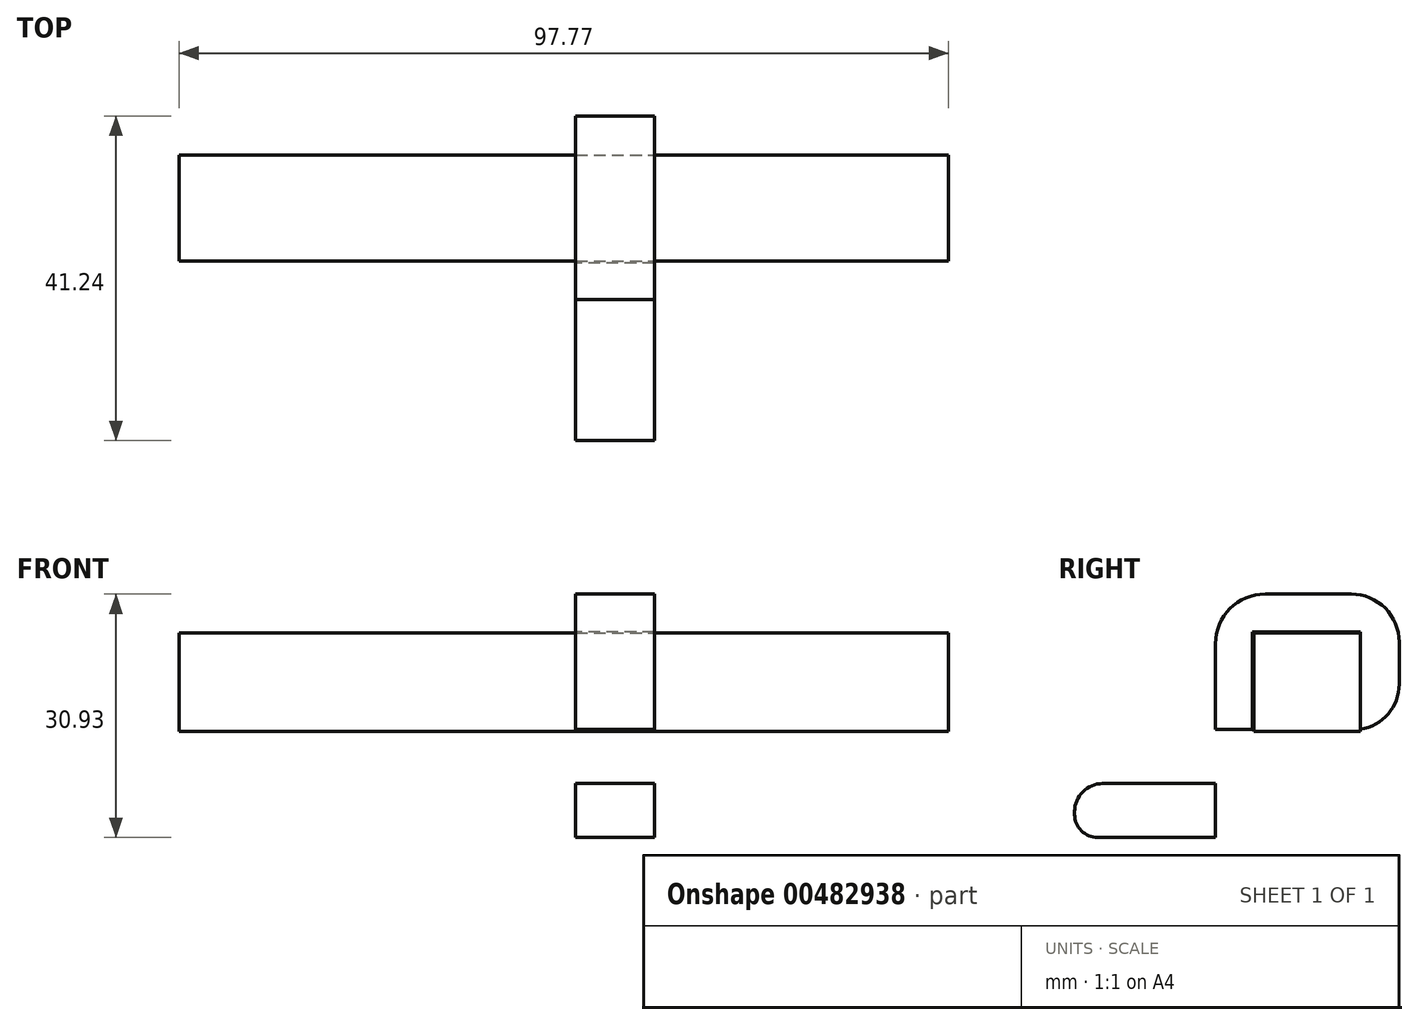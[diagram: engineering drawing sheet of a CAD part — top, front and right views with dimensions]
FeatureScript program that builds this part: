
annotation { "Feature Type Name" : "Feature", "Feature Type Description" : "" }
export const myFeature = defineFeature(function(context is Context, id is Id, definition is map)
    precondition{}
    {
        {
            var Q0;
            Q0=qCreatedBy(makeId("Front.planeOp"),FACE);
            var sketch = newSketch(context, id + "F0", { "sketchPlane" : qUnion([Q0])});
            skLineSegment(sketch, "E0.bottom", {"start": v(-50.4, 26) * mm, "end": v(47.37, 26) * mm});
            skLineSegment(sketch, "E0.top", {"start": v(-50.4, 0) * mm, "end": v(47.37, 0) * mm});
            skLineSegment(sketch, "E0.left", {"start": v(-50.4, 26) * mm, "end": v(-50.4, 0) * mm});
            skLineSegment(sketch, "E0.right", {"start": v(47.37, 26) * mm, "end": v(47.37, 0) * mm});
            skLineSegment(sketch, "E1", {"start": v(47.37, 13.5) * mm, "end": v(-50.4, 13.5) * mm});
            skPoint(sketch, "E1.endSnap0", {"position": v(-50.4, 13) * mm});
            skSolve(sketch);
        }
        {
            var Q0;
            Q0=makeQuery(id+"F0.imprint","IMPRINT",FACE,{"disambiguationData":[TD([[makeQuery(id+"F0.imprint","IMPRINT",EDGE,{"derivedFrom":sQuery(id+"F0.wireOp",EDGE,"E0.bottom")}),-1.0]])]});
            extrude(context, id + "F1", {"entities" : qUnion([Q0]), "depth" : 13.5 * mm});
        }
        {
            var Q0;
            Q0=qCreatedBy(makeId("Right.planeOp"),FACE);
            var sketch = newSketch(context, id + "F2", { "sketchPlane" : qUnion([Q0])});
            skLineSegment(sketch, "E2.bottom", {"start": v(-1.15, 30.93) * mm, "end": v(-12.07, 30.93) * mm});
            skLineSegment(sketch, "E2.top", {"start": v(-0.81, 13.72) * mm, "end": v(-18.39, 13.72) * mm});
            skLineSegment(sketch, "E2.left", {"start": v(4.96, 24.82) * mm, "end": v(4.96, 19.49) * mm});
            skLineSegment(sketch, "E2.right", {"start": v(-18.39, 24.62) * mm, "end": v(-18.39, 13.72) * mm});
            skLineSegment(sketch, "E3.bottom", {"start": v(-18.39, 13.72) * mm, "end": v(-13.72, 13.72) * mm});
            skLineSegment(sketch, "E3.top", {"start": v(-18.39, 0) * mm, "end": v(-13.72, 0) * mm});
            skLineSegment(sketch, "E3.left", {"start": v(-18.39, 13.72) * mm, "end": v(-18.39, 0) * mm});
            skLineSegment(sketch, "E3.right", {"start": v(-13.72, 13.72) * mm, "end": v(-13.72, 0) * mm});
            skPoint(sketch, "E4.oppositeSnap0", {"position": v(-18.39, 6.86) * mm});
            skLineSegment(sketch, "E4.bottom", {"start": v(-18.39, 0) * mm, "end": v(-33.34, 0) * mm});
            skLineSegment(sketch, "E4.top", {"start": v(-18.39, 6.86) * mm, "end": v(-32.72, 6.86) * mm});
            skLineSegment(sketch, "E4.left", {"start": v(-18.39, 0) * mm, "end": v(-18.39, 6.86) * mm});
            skLineSegment(sketch, "E4.right", {"start": v(-36.28, 2.94) * mm, "end": v(-36.28, 3.3) * mm});
            skPoint(sketch, "E5.visualSharp", {"position": v(4.96, 30.93) * mm});
            skArc(sketch, "E5.filletArc", {"start": v(4.96, 24.82) * mm, "mid": v(3.17, 29.14) * mm, "end": v(-1.15, 30.93) * mm});
            skPoint(sketch, "E6.visualSharp", {"position": v(-18.39, 30.93) * mm});
            skArc(sketch, "E6.filletArc", {"start": v(-12.07, 30.93) * mm, "mid": v(-16.53, 29.08) * mm, "end": v(-18.39, 24.62) * mm});
            skPoint(sketch, "E7.visualSharp", {"position": v(-36.28, 6.86) * mm});
            skArc(sketch, "E7.filletArc", {"start": v(-32.72, 6.86) * mm, "mid": v(-35.24, 5.81) * mm, "end": v(-36.28, 3.3) * mm});
            skPoint(sketch, "E8.visualSharp", {"position": v(-36.28, 0) * mm});
            skArc(sketch, "E8.filletArc", {"start": v(-36.28, 2.94) * mm, "mid": v(-35.42, 0.86) * mm, "end": v(-33.34, 0) * mm});
            skLineSegment(sketch, "E9.bottom", {"start": v(0, 13.72) * mm, "end": v(-13.7, 13.72) * mm});
            skLineSegment(sketch, "E9.top", {"start": v(0, 26.14) * mm, "end": v(-13.7, 26.14) * mm});
            skLineSegment(sketch, "E9.left", {"start": v(0, 13.72) * mm, "end": v(0, 26.14) * mm});
            skLineSegment(sketch, "E9.right", {"start": v(-13.7, 13.72) * mm, "end": v(-13.7, 26.14) * mm});
            skPoint(sketch, "E10.visualSharp", {"position": v(4.96, 13.72) * mm});
            skArc(sketch, "E10.filletArc", {"start": v(-0.81, 13.72) * mm, "mid": v(3.27, 15.4) * mm, "end": v(4.96, 19.49) * mm});
            skSolve(sketch);
        }
        {
            var Q0;
            Q0=makeQuery(id+"F2.imprint","IMPRINT",FACE,{"disambiguationData":[TD([[makeQuery(id+"F2.imprint","IMPRINT",EDGE,{"derivedFrom":sQuery(id+"F2.wireOp",EDGE,"E2.bottom")}),1.0]])]});
            var Q1;
            Q1=makeQuery(id+"F2.imprint","IMPRINT",FACE,{"disambiguationData":[TD([[makeQuery(id+"F2.imprint","IMPRINT",EDGE,{"derivedFrom":sQuery(id+"F2.wireOp",EDGE,"E3.bottom")}),-1.0]])]});
            var Q2;
            Q2=makeQuery(id+"F2.imprint","IMPRINT",FACE,{"disambiguationData":[TD([[makeQuery(id+"F2.imprint","IMPRINT",EDGE,{"derivedFrom":sQuery(id+"F2.wireOp",EDGE,"E4.bottom")}),-1.0]])]});
            extrude(context, id + "F3", {"entities" : qUnion([Q0, Q1, Q2]), "operationType" : NewBodyOperationType.ADD, "depth" : 10 * mm});
        }
    });
